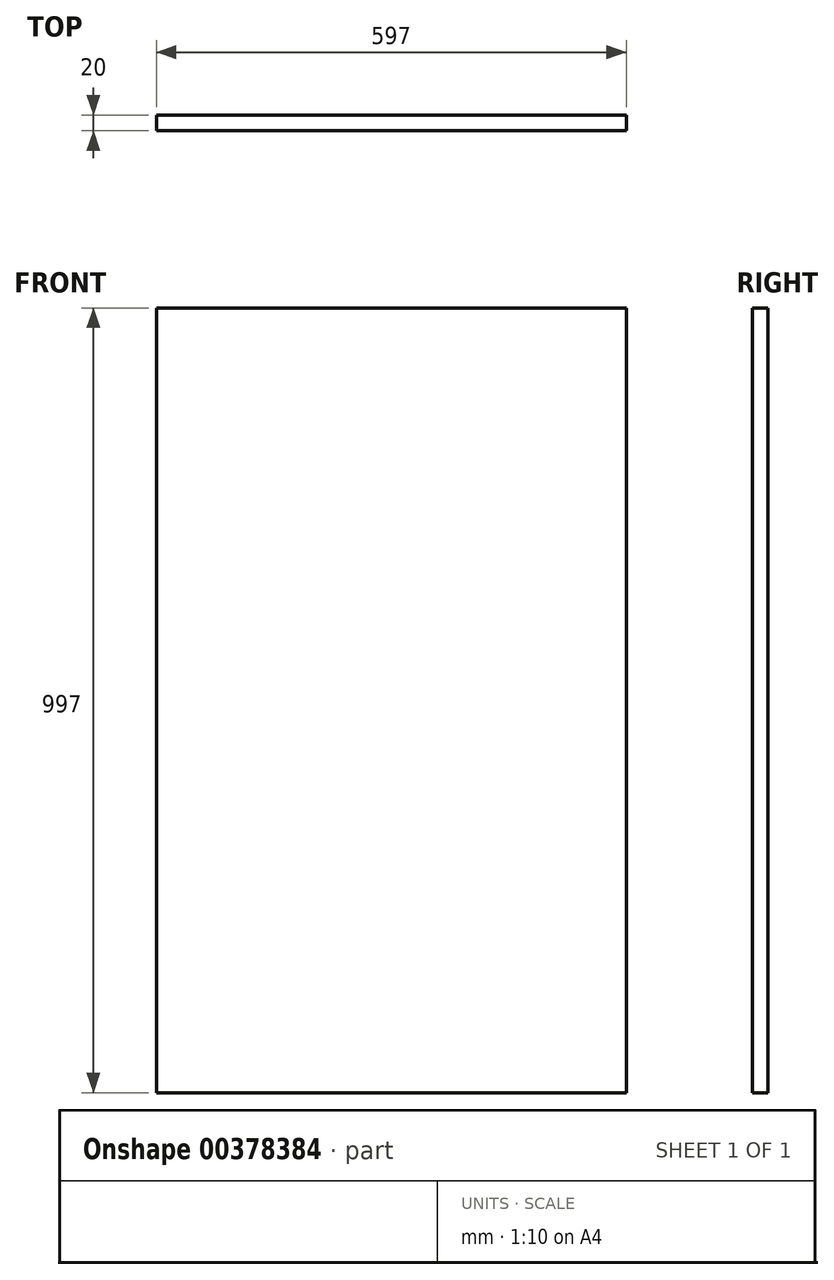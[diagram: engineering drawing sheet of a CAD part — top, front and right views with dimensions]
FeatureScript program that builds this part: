
annotation { "Feature Type Name" : "Feature", "Feature Type Description" : "" }
export const myFeature = defineFeature(function(context is Context, id is Id, definition is map)
    precondition{}
    {
        {
            var Q0;
            Q0=qCreatedBy(makeId("Front.planeOp"),FACE);
            var sketch = newSketch(context, id + "F0", { "sketchPlane" : qUnion([Q0])});
            skLineSegment(sketch, "E0.bottom", {"start": v(298.5, 498.5) * mm, "end": v(-298.5, 498.5) * mm});
            skLineSegment(sketch, "E0.top", {"start": v(298.5, -498.5) * mm, "end": v(-298.5, -498.5) * mm});
            skLineSegment(sketch, "E0.left", {"start": v(298.5, 498.5) * mm, "end": v(298.5, -498.5) * mm});
            skLineSegment(sketch, "E0.right", {"start": v(-298.5, 498.5) * mm, "end": v(-298.5, -498.5) * mm});
            skPoint(sketch, "E0.middle", {"position": v(0, 0) * mm});
            skSolve(sketch);
        }
        {
            var Q0;
            Q0 = qSketchRegion(id + "F0", true);
            extrude(context, id + "F1", {"entities" : qUnion([Q0]), "depth" : 20 * mm});
        }
    });
